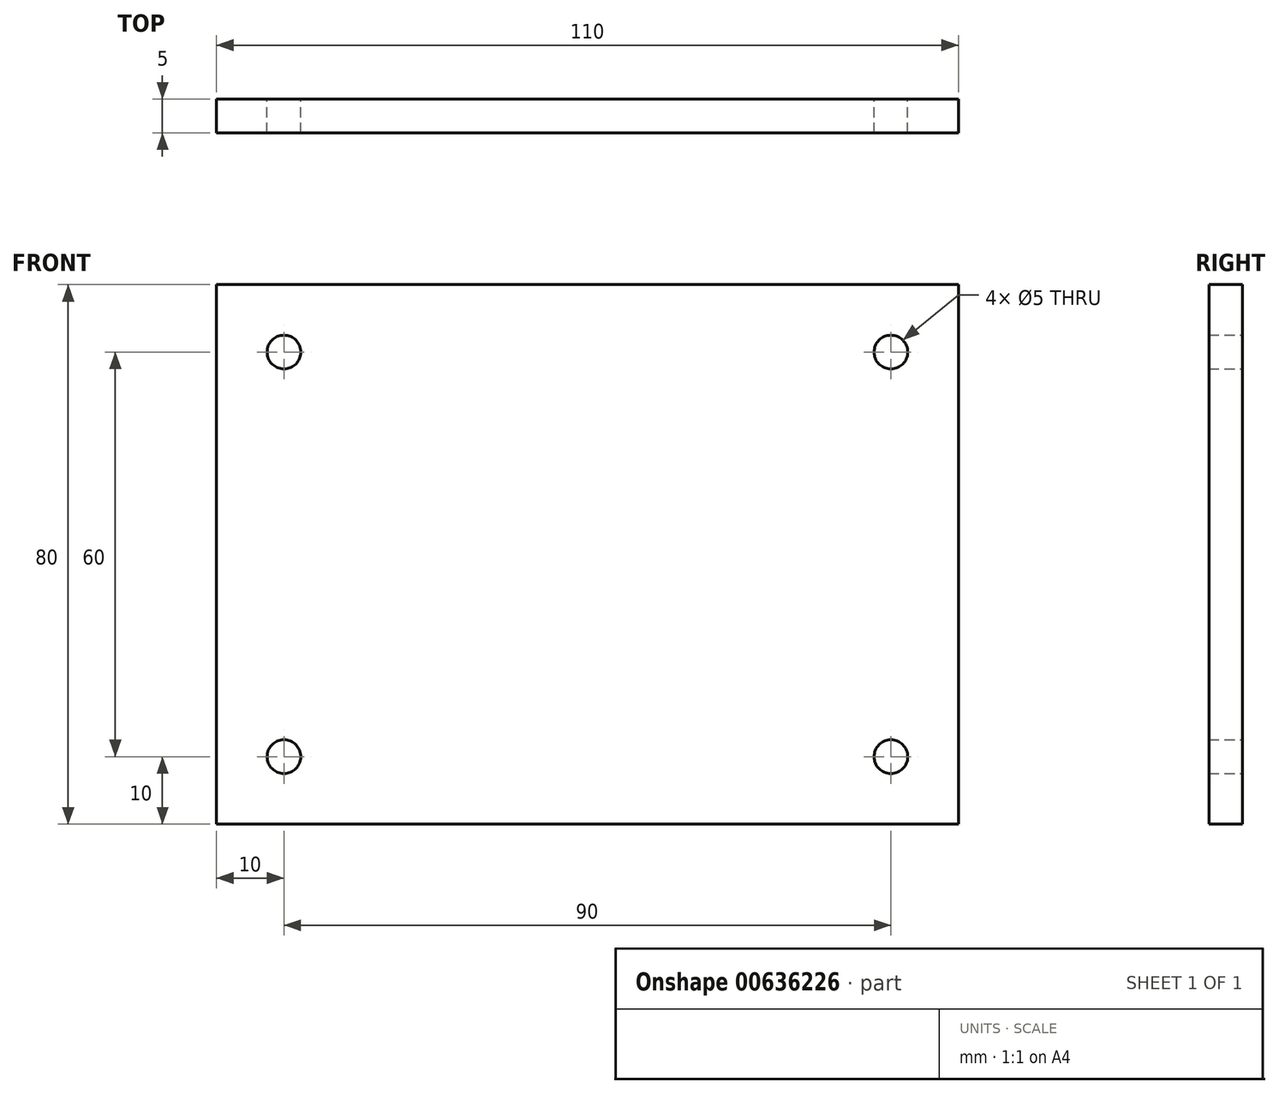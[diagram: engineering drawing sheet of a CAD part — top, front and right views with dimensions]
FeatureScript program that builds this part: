
annotation { "Feature Type Name" : "Feature", "Feature Type Description" : "" }
export const myFeature = defineFeature(function(context is Context, id is Id, definition is map)
    precondition{}
    {
        {
            var Q0;
            Q0=qCreatedBy(makeId("Front.planeOp"),FACE);
            var sketch = newSketch(context, id + "F0", { "sketchPlane" : qUnion([Q0])});
            skLineSegment(sketch, "E0.bottom", {"start": v(0, 0) * mm, "end": v(110, 0) * mm});
            skLineSegment(sketch, "E0.top", {"start": v(0, 80) * mm, "end": v(110, 80) * mm});
            skLineSegment(sketch, "E0.left", {"start": v(0, 0) * mm, "end": v(0, 80) * mm});
            skLineSegment(sketch, "E0.right", {"start": v(110, 0) * mm, "end": v(110, 80) * mm});
            skCircle(sketch, "E1", {"center": v(10, 70) * mm, "radius": 2.5 * mm});
            skCircle(sketch, "E2.MirrorC", {"center": v(100, 70) * mm, "radius": 2.5 * mm});
            skCircle(sketch, "E3.MirrorC", {"center": v(10, 10) * mm, "radius": 2.5 * mm});
            skCircle(sketch, "E4.MirrorC", {"center": v(100, 10) * mm, "radius": 2.5 * mm});
            skSolve(sketch);
        }
        {
            var Q0;
            Q0 = qSketchRegion(id + "F0", true);
            extrude(context, id + "F1", {"entities" : qUnion([Q0]), "depth" : 5 * mm, "offsetDistance" : 25.4 * mm});
        }
    });
